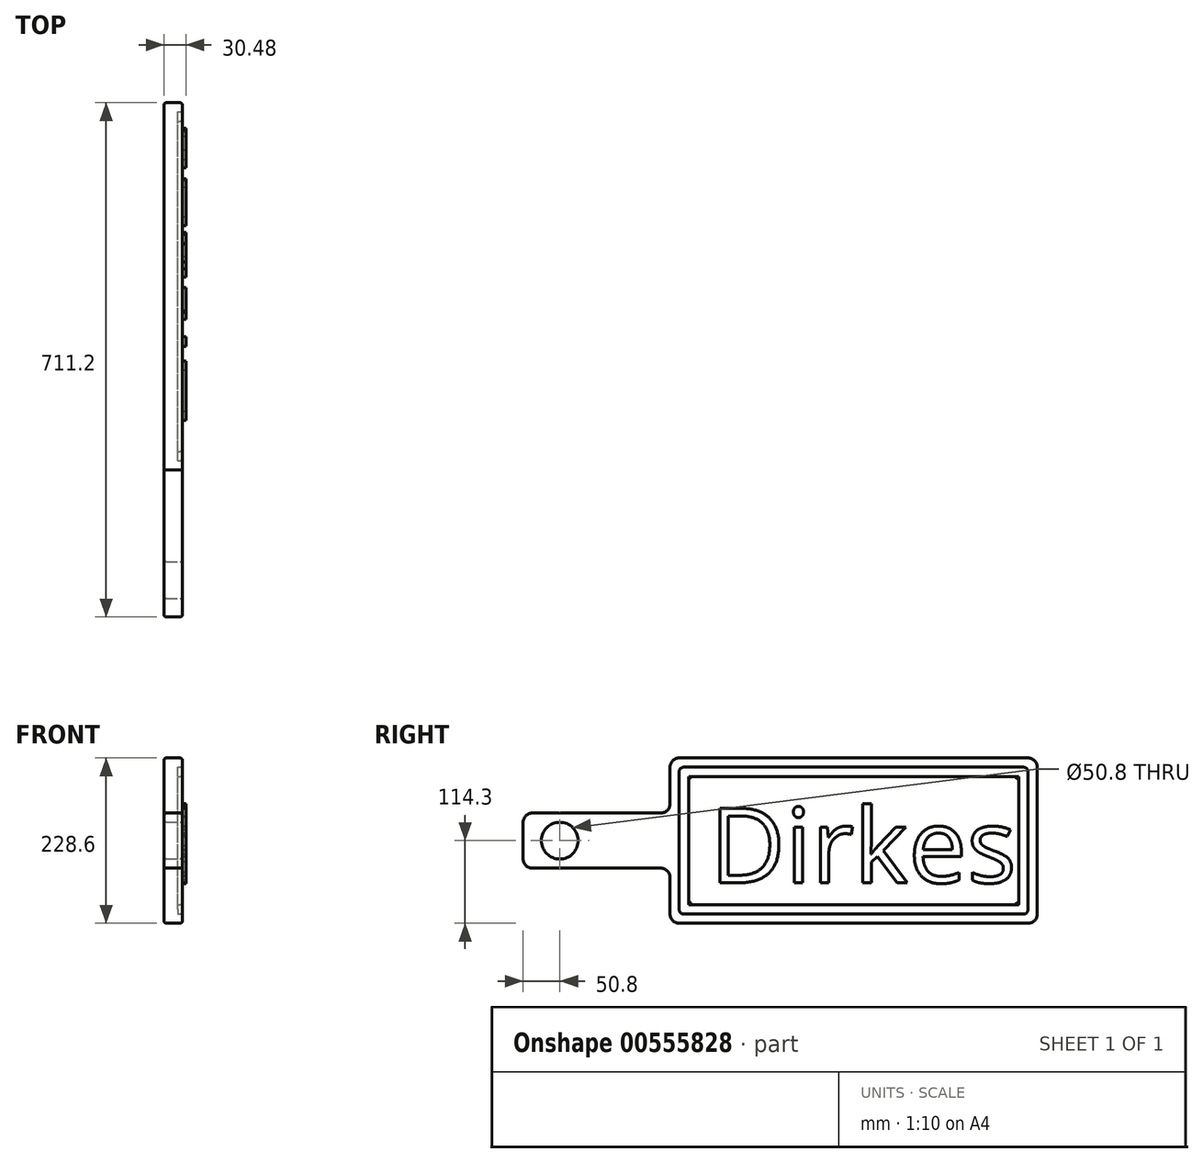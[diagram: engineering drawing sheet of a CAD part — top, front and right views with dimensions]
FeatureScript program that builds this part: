
annotation { "Feature Type Name" : "Feature", "Feature Type Description" : "" }
export const myFeature = defineFeature(function(context is Context, id is Id, definition is map)
    precondition{}
    {
        {
            var Q0;
            Q0=qCreatedBy(makeId("Right.planeOp"),FACE);
            var sketch = newSketch(context, id + "F0", { "sketchPlane" : qUnion([Q0])});
            skLineSegment(sketch, "E0.bottom", {"start": v(0, 0) * mm, "end": v(508, 0) * mm});
            skLineSegment(sketch, "E0.top", {"start": v(0, 228.6) * mm, "end": v(508, 228.6) * mm});
            skLineSegment(sketch, "E0.left", {"start": v(0, 0) * mm, "end": v(0, 228.6) * mm});
            skLineSegment(sketch, "E0.right", {"start": v(508, 0) * mm, "end": v(508, 228.6) * mm});
            skLineSegment(sketch, "E1.bottom", {"start": v(0, 152.4) * mm, "end": v(-203.2, 152.4) * mm});
            skLineSegment(sketch, "E1.top", {"start": v(0, 76.2) * mm, "end": v(-203.2, 76.2) * mm});
            skLineSegment(sketch, "E1.left", {"start": v(0, 152.4) * mm, "end": v(0, 76.2) * mm});
            skLineSegment(sketch, "E1.right", {"start": v(-203.2, 152.4) * mm, "end": v(-203.2, 76.2) * mm});
            skSolve(sketch);
        }
        {
            var Q0;
            {var subQ3=sQuery(id+"F0.wireOp",EDGE,"E0.bottom");Q0=makeQuery(id+"F0.imprint","IMPRINT",FACE,{"disambiguationData":[TD([[makeQuery(id+"F0.imprint","IMPRINT",EDGE,{"derivedFrom":subQ3}),1.0]])]});}
            var Q1;
            Q1=makeQuery(id+"F0.imprint","IMPRINT",FACE,{"disambiguationData":[TD([[makeQuery(id+"F0.imprint","IMPRINT",EDGE,{"derivedFrom":sQuery(id+"F0.wireOp",EDGE,"E1.bottom")}),1.0]])]});
            extrude(context, id + "F1", {"entities" : qUnion([Q0, Q1]), "depth" : 25.4 * mm, "offsetDistance" : 25.4 * mm});
        }
        {
            var Q0;
            Q0=makeQuery(id+"F1.opExtrude","CAP_FACE",FACE,{"disambiguationData":[OSD([sQuery(id+"F0.wireOp",EDGE,"E0.bottom"),sQuery(id+"F0.wireOp",EDGE,"E0.top"),sQuery(id+"F0.wireOp",EDGE,"E0.left"),sQuery(id+"F0.wireOp",EDGE,"E0.right"),sQuery(id+"F0.wireOp",EDGE,"E1.bottom"),sQuery(id+"F0.wireOp",EDGE,"E1.top"),sQuery(id+"F0.wireOp",EDGE,"E1.right")])],"isStart":false});
            var sketch = newSketch(context, id + "F2", { "sketchPlane" : qUnion([Q0])});
            skCircle(sketch, "E2", {"center": v(-152.4, 114.3) * mm, "radius": 25.4 * mm});
            skSolve(sketch);
        }
        {
            var Q0;
            Q0 = qSketchRegion(id + "F2", true);
            extrude(context, id + "F3", {"entities" : qUnion([Q0]), "operationType" : NewBodyOperationType.REMOVE, "oppositeDirection" : true, "depth" : 25.4 * mm, "offsetDistance" : 25.4 * mm});
        }
        {
            var Q0;
            Q0=makeQuery(id+"F1.opExtrude","CAP_FACE",FACE,{"disambiguationData":[OSD([sQuery(id+"F0.wireOp",EDGE,"E0.bottom"),sQuery(id+"F0.wireOp",EDGE,"E0.top"),sQuery(id+"F0.wireOp",EDGE,"E0.left"),sQuery(id+"F0.wireOp",EDGE,"E0.right"),sQuery(id+"F0.wireOp",EDGE,"E1.bottom"),sQuery(id+"F0.wireOp",EDGE,"E1.top"),sQuery(id+"F0.wireOp",EDGE,"E1.right")])],"isStart":false});
            var sketch = newSketch(context, id + "F4", { "sketchPlane" : qUnion([Q0])});
            skLineSegment(sketch, "E3.0", {"start": v(12.7, 12.7) * mm, "end": v(12.7, 76.2) * mm});
            skLineSegment(sketch, "E3.1", {"start": v(12.7, 152.4) * mm, "end": v(12.7, 215.9) * mm});
            skLineSegment(sketch, "E3.2", {"start": v(12.7, 215.9) * mm, "end": v(495.3, 215.9) * mm});
            skLineSegment(sketch, "E3.3", {"start": v(495.3, 12.7) * mm, "end": v(495.3, 215.9) * mm});
            skLineSegment(sketch, "E3.4", {"start": v(12.7, 12.7) * mm, "end": v(495.3, 12.7) * mm});
            skLineSegment(sketch, "E4", {"start": v(12.7, 152.4) * mm, "end": v(12.7, 76.2) * mm});
            skLineSegment(sketch, "E5.0", {"start": v(25.65, 152.4) * mm, "end": v(25.65, 202.95) * mm});
            skLineSegment(sketch, "E5.1", {"start": v(482.35, 25.65) * mm, "end": v(482.35, 202.95) * mm});
            skLineSegment(sketch, "E5.2", {"start": v(25.65, 25.65) * mm, "end": v(482.35, 25.65) * mm});
            skLineSegment(sketch, "E5.3", {"start": v(25.65, 202.95) * mm, "end": v(482.35, 202.95) * mm});
            skLineSegment(sketch, "E5.4", {"start": v(25.65, 25.65) * mm, "end": v(25.65, 76.2) * mm});
            skLineSegment(sketch, "E5.5", {"start": v(25.65, 152.4) * mm, "end": v(25.65, 76.2) * mm});
            skSolve(sketch);
        }
        {
            var Q0;
            Q0=makeQuery(id+"F4.imprint","IMPRINT",FACE,{"disambiguationData":[TD([[makeQuery(id+"F4.imprint","IMPRINT",EDGE,{"derivedFrom":sQuery(id+"F4.wireOp",EDGE,"E3.0")}),-1.0]])]});
            extrude(context, id + "F5", {"entities" : qUnion([Q0]), "operationType" : NewBodyOperationType.REMOVE, "oppositeDirection" : true, "depth" : 6.35 * mm, "offsetDistance" : 25.4 * mm});
        }
        {
            var Q0;
            Q0=makeQuery(id+"F5.boolean.opBoolean","COPY",EDGE,{"derivedFrom":makeQuery(id+"F5.opExtrude","SWEPT_EDGE",EDGE,{"disambiguationData":[OSD([sQuery(id+"F4.wireOp",EDGE,"E3.1"),sQuery(id+"F4.wireOp",EDGE,"E3.2")])]})});
            fillet(context, id + "F6", {"entities" : qUnion([Q0]), "radius" : 6.35 * mm, "tangentPropagation" : true, "allowEdgeOverflow" : false});
        }
        {
            var Q0;
            Q0=makeQuery(id+"F5.boolean.opBoolean","COPY",EDGE,{"derivedFrom":makeQuery(id+"F5.opExtrude","SWEPT_EDGE",EDGE,{"disambiguationData":[OSD([sQuery(id+"F4.wireOp",EDGE,"E3.2"),sQuery(id+"F4.wireOp",EDGE,"E3.3")])]})});
            fillet(context, id + "F7", {"entities" : qUnion([Q0]), "radius" : 6.35 * mm, "tangentPropagation" : true, "allowEdgeOverflow" : false});
        }
        {
            var Q0;
            Q0=makeQuery(id+"F5.boolean.opBoolean","COPY",EDGE,{"derivedFrom":makeQuery(id+"F5.opExtrude","SWEPT_EDGE",EDGE,{"disambiguationData":[OSD([sQuery(id+"F4.wireOp",EDGE,"E3.3"),sQuery(id+"F4.wireOp",EDGE,"E3.4")])]})});
            var Q1;
            Q1=makeQuery(id+"F5.boolean.opBoolean","COPY",EDGE,{"derivedFrom":makeQuery(id+"F5.opExtrude","SWEPT_EDGE",EDGE,{"disambiguationData":[OSD([sQuery(id+"F4.wireOp",EDGE,"E3.0"),sQuery(id+"F4.wireOp",EDGE,"E3.4")])]})});
            fillet(context, id + "F8", {"entities" : qUnion([Q0, Q1]), "radius" : 6.35 * mm, "tangentPropagation" : true, "allowEdgeOverflow" : false});
        }
        {
            var Q0;
            Q0=makeQuery(id+"F1.opExtrude","SWEPT_EDGE",EDGE,{"disambiguationData":[OSD([sQuery(id+"F0.wireOp",EDGE,"E0.top"),sQuery(id+"F0.wireOp",EDGE,"E0.left")])]});
            var Q1;
            Q1=makeQuery(id+"F1.opExtrude","SWEPT_EDGE",EDGE,{"disambiguationData":[OSD([sQuery(id+"F0.wireOp",EDGE,"E1.bottom"),sQuery(id+"F0.wireOp",EDGE,"E1.right")])]});
            var Q2;
            Q2=makeQuery(id+"F1.opExtrude","SWEPT_EDGE",EDGE,{"disambiguationData":[OSD([sQuery(id+"F0.wireOp",EDGE,"E0.bottom"),sQuery(id+"F0.wireOp",EDGE,"E0.left")])]});
            var Q3;
            Q3=makeQuery(id+"F1.opExtrude","SWEPT_EDGE",EDGE,{"disambiguationData":[OSD([sQuery(id+"F0.wireOp",EDGE,"E1.top"),sQuery(id+"F0.wireOp",EDGE,"E1.right")])]});
            var Q4;
            Q4=makeQuery(id+"F1.opExtrude","SWEPT_EDGE",EDGE,{"disambiguationData":[OSD([sQuery(id+"F0.wireOp",EDGE,"E0.left"),sQuery(id+"F0.wireOp",EDGE,"E1.top"),sQuery(id+"F0.wireOp",EDGE,"E1.left")])]});
            var Q5;
            Q5=makeQuery(id+"F1.opExtrude","SWEPT_EDGE",EDGE,{"disambiguationData":[OSD([sQuery(id+"F0.wireOp",EDGE,"E0.left"),sQuery(id+"F0.wireOp",EDGE,"E1.bottom"),sQuery(id+"F0.wireOp",EDGE,"E1.left")])]});
            var Q6;
            Q6=makeQuery(id+"F1.opExtrude","SWEPT_EDGE",EDGE,{"disambiguationData":[OSD([sQuery(id+"F0.wireOp",EDGE,"E0.bottom"),sQuery(id+"F0.wireOp",EDGE,"E0.right")])]});
            var Q7;
            Q7=makeQuery(id+"F1.opExtrude","SWEPT_EDGE",EDGE,{"disambiguationData":[OSD([sQuery(id+"F0.wireOp",EDGE,"E0.top"),sQuery(id+"F0.wireOp",EDGE,"E0.right")])]});
            fillet(context, id + "F9", {"entities" : qUnion([Q0, Q1, Q2, Q3, Q4, Q5, Q6, Q7]), "radius" : 12.7 * mm, "tangentPropagation" : true, "allowEdgeOverflow" : false});
        }
        {
            var Q0;
            Q0=makeQuery(id+"F5.boolean.opBoolean","SPLIT",FACE,{"disambiguationData":[TD([makeQuery(id+"F5.opExtrude","SWEPT_FACE",FACE,{"disambiguationData":[OSD([sQuery(id+"F4.wireOp",EDGE,"E5.1")])]})])],"derivedFrom":makeQuery(id+"F1.opExtrude","CAP_FACE",FACE,{"disambiguationData":[OSD([sQuery(id+"F0.wireOp",EDGE,"E0.bottom"),sQuery(id+"F0.wireOp",EDGE,"E0.top"),sQuery(id+"F0.wireOp",EDGE,"E0.left"),sQuery(id+"F0.wireOp",EDGE,"E0.right"),sQuery(id+"F0.wireOp",EDGE,"E1.bottom"),sQuery(id+"F0.wireOp",EDGE,"E1.top"),sQuery(id+"F0.wireOp",EDGE,"E1.right")])],"isStart":false})});
            var Q1;
            {var subQ0=sQuery(id+"F0.wireOp",EDGE,"E1.right");var subQ1=sQuery(id+"F0.wireOp",EDGE,"E1.top");var subQ2=sQuery(id+"F0.wireOp",EDGE,"E1.bottom");var subQ3=sQuery(id+"F0.wireOp",EDGE,"E0.right");var subQ4=sQuery(id+"F0.wireOp",EDGE,"E0.bottom");var subQ5=sQuery(id+"F0.wireOp",EDGE,"E0.left");var subQ6=sQuery(id+"F0.wireOp",EDGE,"E0.top");Q1=makeQuery(id+"F5.boolean.opBoolean","SPLIT",FACE,{"disambiguationData":[TD([makeQuery(id+"F1.opExtrude","SWEPT_FACE",FACE,{"disambiguationData":[OSD([subQ4])]})])],"derivedFrom":makeQuery(id+"F1.opExtrude","CAP_FACE",FACE,{"disambiguationData":[OSD([subQ4,subQ6,subQ5,subQ3,subQ2,subQ1,subQ0])],"isStart":false})});}
            var Q2;
            Q2=makeQuery(id+"F1.opExtrude","CAP_FACE",FACE,{"disambiguationData":[OSD([sQuery(id+"F0.wireOp",EDGE,"E0.bottom"),sQuery(id+"F0.wireOp",EDGE,"E0.top"),sQuery(id+"F0.wireOp",EDGE,"E0.left"),sQuery(id+"F0.wireOp",EDGE,"E0.right"),sQuery(id+"F0.wireOp",EDGE,"E1.bottom"),sQuery(id+"F0.wireOp",EDGE,"E1.top"),sQuery(id+"F0.wireOp",EDGE,"E1.right")])],"isStart":true});
            fillet(context, id + "F10", {"entities" : qUnion([Q0, Q1, Q2]), "radius" : 3.17 * mm, "tangentPropagation" : true, "allowEdgeOverflow" : false});
        }
        {
            var Q0;
            Q0=makeQuery(id+"F5.boolean.opBoolean","SPLIT",FACE,{"disambiguationData":[TD([makeQuery(id+"F5.opExtrude","SWEPT_FACE",FACE,{"disambiguationData":[OSD([sQuery(id+"F4.wireOp",EDGE,"E5.1")])]})])],"derivedFrom":makeQuery(id+"F1.opExtrude","CAP_FACE",FACE,{"disambiguationData":[OSD([sQuery(id+"F0.wireOp",EDGE,"E0.bottom"),sQuery(id+"F0.wireOp",EDGE,"E0.top"),sQuery(id+"F0.wireOp",EDGE,"E0.left"),sQuery(id+"F0.wireOp",EDGE,"E0.right"),sQuery(id+"F0.wireOp",EDGE,"E1.bottom"),sQuery(id+"F0.wireOp",EDGE,"E1.top"),sQuery(id+"F0.wireOp",EDGE,"E1.right")])],"isStart":false})});
            var sketch = newSketch(context, id + "F11", { "sketchPlane" : qUnion([Q0])});
            skText(sketch, "E6", { "text": "Dirkes", "fontName": "OpenSans-Regular.ttf"});
            const initialGuessF11  = {"E6": [0.0547, 0.0562, 1, 0, 0.10346]};
            skSetInitialGuess(sketch, initialGuessF11);
            skSolve(sketch);
        }
        {
            var Q0;
            Q0 = qSketchRegion(id + "F11", true);
            extrude(context, id + "F12", {"entities" : qUnion([Q0]), "operationType" : NewBodyOperationType.ADD, "depth" : 5.08 * mm, "offsetDistance" : 25.4 * mm});
        }
    });
